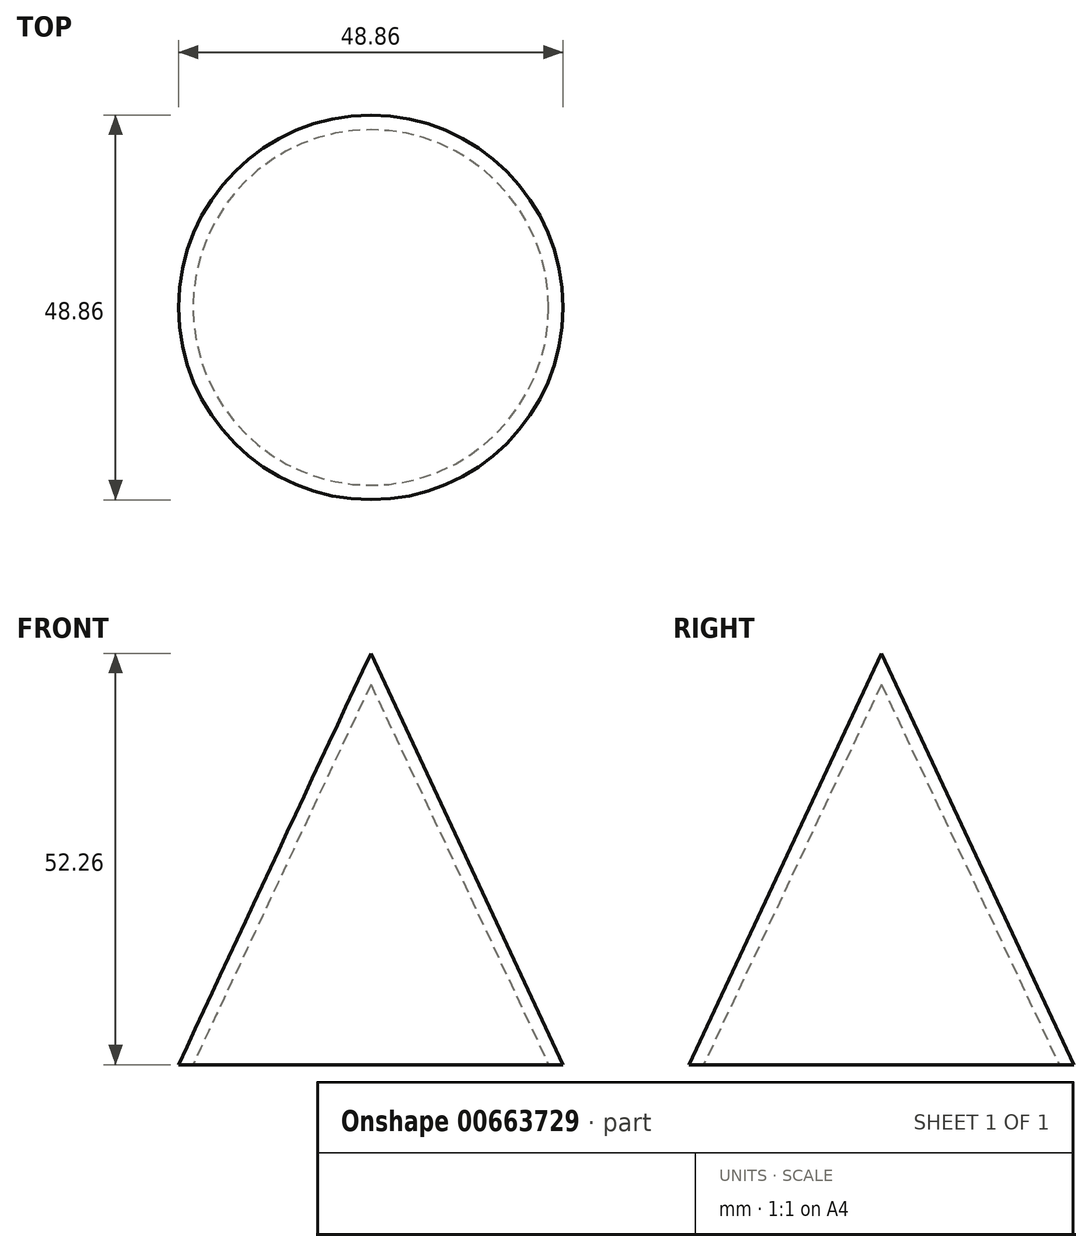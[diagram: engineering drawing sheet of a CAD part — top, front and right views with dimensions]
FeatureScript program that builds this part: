
annotation { "Feature Type Name" : "Feature", "Feature Type Description" : "" }
export const myFeature = defineFeature(function(context is Context, id is Id, definition is map)
    precondition{}
    {
        {
            var Q0;
            Q0=qCreatedBy(makeId("Front.planeOp"),FACE);
            var sketch = newSketch(context, id + "F0", { "sketchPlane" : qUnion([Q0])});
            skLineSegment(sketch, "E0", {"start": v(0, 0) * mm, "end": v(0, 52.26) * mm});
            skLineSegment(sketch, "E1", {"start": v(0, 52.26) * mm, "end": v(24.43, 0) * mm});
            skLineSegment(sketch, "E2", {"start": v(24.43, 0) * mm, "end": v(0, 0) * mm});
            skLineSegment(sketch, "E3", {"start": v(22.58, 0) * mm, "end": v(0, 48.32) * mm});
            skSolve(sketch);
        }
        {
            var Q0;
            {var subQ0=sQuery(id+"F0.wireOp",EDGE,"E1");Q0=makeQuery(id+"F0.imprint","IMPRINT",FACE,{"disambiguationData":[TD([[makeQuery(id+"F0.imprint","IMPRINT",EDGE,{"derivedFrom":subQ0}),-1.0]])]});}
            var Q1;
            Q1=sQuery(id+"F0.wireOp",EDGE,"E0");
            revolve(context, id + "F1", {"entities" : qUnion([Q0]), "axis" : qUnion([Q1]), "revolveType" : RevolveType.FULL});
        }
    });
